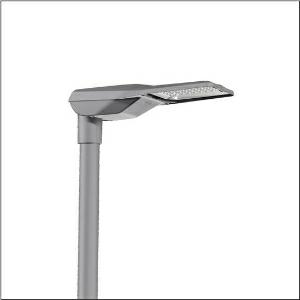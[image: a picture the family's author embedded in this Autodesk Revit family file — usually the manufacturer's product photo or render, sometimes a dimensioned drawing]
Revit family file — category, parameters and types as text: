
# Revit family: streetlight_sl_21_iq_mini___pl52_5xe2h41d08hb_c209
name_source: partatom
category: Lighting Fixtures
units: mm (PartAtom-declared; Revit-internal decimal feet)

## family parameters
Cut with Voids When Loaded = No
Host = Face
Light Source = No
Part Type = Normal
Room Calculation Point = No
Round Connector Dimension = Use Diameter
Shared = No

## types (1)
- --- (1 x LED, 9690 lm, 70.9 W, 4000K)
    Apparent Load = 71 VA
    CIE Flux Codes = 27 59 98 100 100
    Color Rendering = 70
    Color Temperature = 4000K
    Default Elevation = 1800 mm
    Description = Streetlight SL 21 iQ mini, mast luminaire, primary light control with lens, of PMMA, primary optical cover: cover, of toughened safety glass, transparent, light distribution: PL52, light emission: direct distribution, primary light characteristic: asymmetric, installation type: post-top, side-entry, LED, High Power LED, rated luminous flux: 9.690lm, luminous efficacy: 137lm/W, light colour: 740, colour temperature: 4000K, control gear: iQ-Comfort, control: Auto-Match, Temp-Guard, Lumen-Switch, Night-Set, Smart-Wire, Light-Fading, Desk-Remote (wireless, voltage-free reading and setting of iQ features in the workshop via application-optimized NFC function/RFID function), optimised constant luminous flux control (CLO 2.0), pre-setting: linear dimming characteristic, mains connection: 220..240V, AC, 50/60Hz, start of lifetime: 71W, end of service life: 75W, reduction: 31W, luminaire housing, of diecast aluminium, powder-coated, Siteco® metallic grey (DB 702S), corrosivity category C5 mid according to DIN EN ISO 12944, please order mast flange separately, inclination adjustable: 0°, 5°, 10°, 15°, sealing non-destructively replaceable, multi-level sealing system, length: 628mm, width: 235mm, height: 110mm, mast flange for spigot size: 42mm (side-entry): 5XC10008XM4, 60/48mm (side-entry/post-top): 5XC10108XM2, 76/60mm (side-entry/post-top): 5XC10108XM1, mounting height: 4..8m, protection rating (complete): IP66, insulation class (complete): insulation class II (safety insulation), certification: CE, ENEC, ENEC+, VDE, impact resistance: IK10, permissible operating ambient temperature for outdoor applications: -40..+50°C, standard-compliant lighting for roads and squares, packaging unit: 1 piece

Light Distribution: PL52
    Height = 110 mm
    Lamp = 1 x LED
    Lamp Light Flux = 9690 lm
    Lamp Power = 70.9 W
    Lamp count = 1
    Length = 625 mm
    Luminous efficacy = 137 lm/W
    Manufacturer = Siteco
    ModVariant = No
    Model = 5XE2H41D08HB
    Number of Poles = 1
    OnlyDefault = Yes
    Power Factor = 1
    Product Name = Streetlight SL 21 iQ mini | PL52
    Product group = mast luminaire | pylon top
    ProductGroupID = 6100
    Protection Class = Protection class II
    Protection Degree = IP 66
    RLX_Detail_Level = 1
    RLX_Emergency_Light_Flux = 0 lm
    RLX_Emergency_Type = 0
    RLX_Emergency_Type_DB = No
    RlxData = <blob elided: 35961 chars, md5=cc9568a1>
    Socket = socket
    Standby Power = 0 W
    System Light Flux = 9690 lm
    System Power = 71 W
    Type Comments = factory setting: luminous flux: 100 % | dim-lin: 254 | 711 mA
    Type Image = l_1003519.jpg
    URL = http://relux.com
    VarID = @adj_158416
    Voltage = 0 V
    Weight = 0.00 kg
    Width = 234 mm

## geometry (parser evidence)
native form markers: Blend x4, Sweep x8
no freeform markers — native parametric forms only
